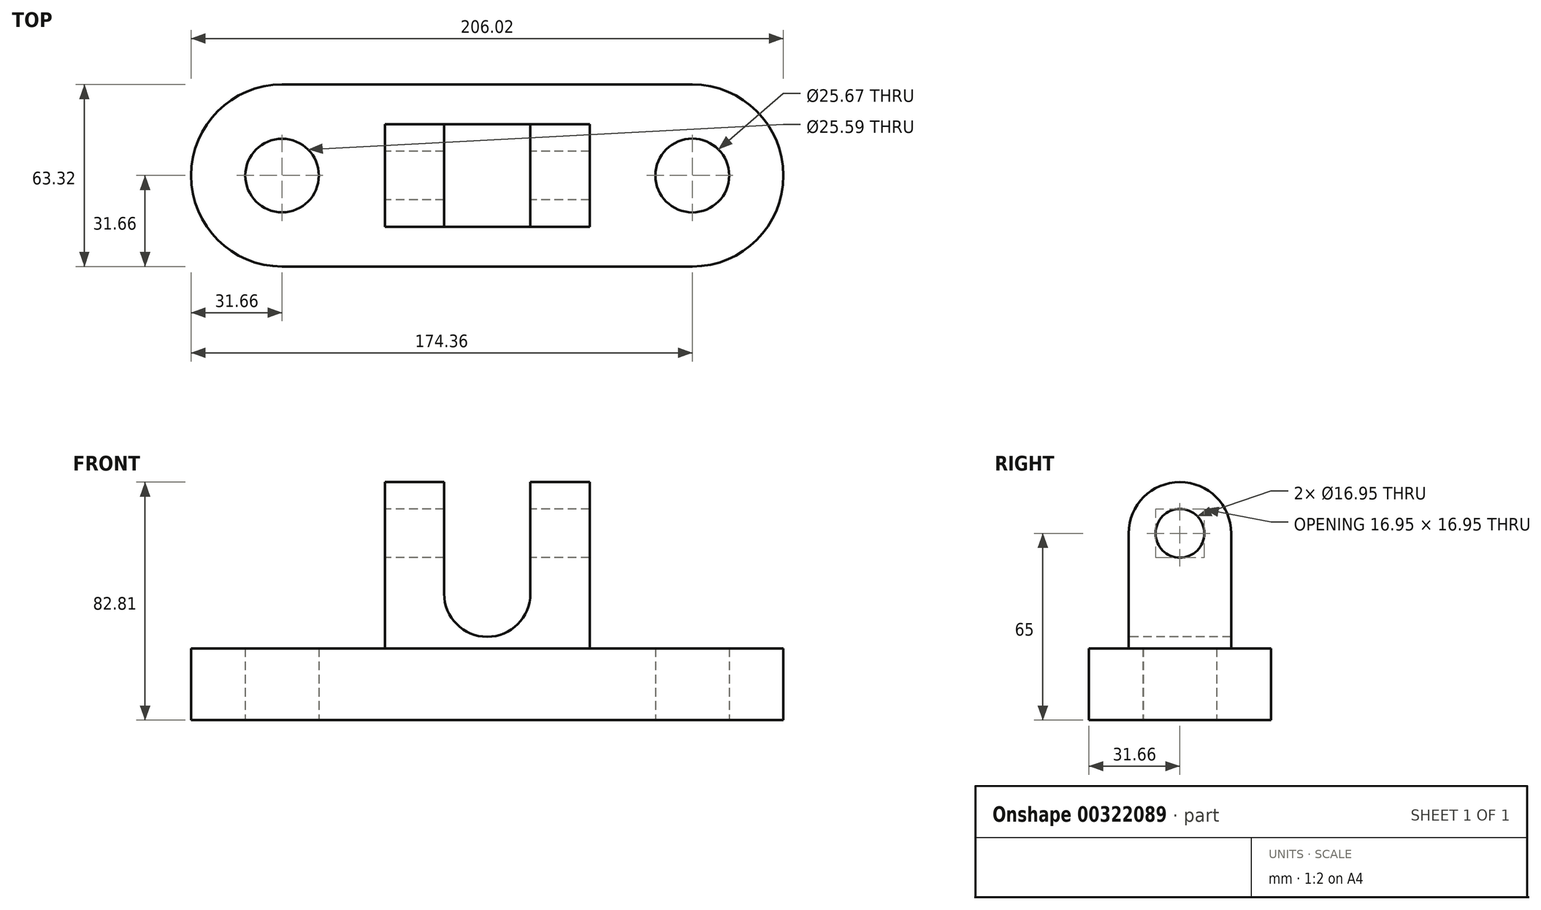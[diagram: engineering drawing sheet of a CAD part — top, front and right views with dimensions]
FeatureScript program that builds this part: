
annotation { "Feature Type Name" : "Feature", "Feature Type Description" : "" }
export const myFeature = defineFeature(function(context is Context, id is Id, definition is map)
    precondition{}
    {
        {
            var Q0;
            Q0=qCreatedBy(makeId("Top.planeOp"),FACE);
            var sketch = newSketch(context, id + "F0", { "sketchPlane" : qUnion([Q0])});
            skLineSegment(sketch, "E0.bottom", {"start": v(-71.35, 31.66) * mm, "end": v(71.35, 31.66) * mm});
            skLineSegment(sketch, "E0.top", {"start": v(-71.35, -31.66) * mm, "end": v(71.35, -31.66) * mm});
            skLineSegment(sketch, "E0.left", {"start": v(-71.35, 31.66) * mm, "end": v(-71.35, -31.66) * mm});
            skLineSegment(sketch, "E0.right", {"start": v(71.35, 31.66) * mm, "end": v(71.35, -31.66) * mm});
            skPoint(sketch, "E0.middle", {"position": v(0, 0) * mm});
            skCircle(sketch, "E1", {"center": v(71.35, 0) * mm, "radius": 31.66 * mm});
            skCircle(sketch, "E2", {"center": v(-71.35, 0) * mm, "radius": 31.66 * mm});
            skCircle(sketch, "E3", {"center": v(71.35, 0) * mm, "radius": 12.83 * mm});
            skCircle(sketch, "E4", {"center": v(-71.35, 0) * mm, "radius": 12.8 * mm});
            skSolve(sketch);
        }
        {
            var Q0;
            Q0 = qSketchRegion(id + "F0", true);
            extrude(context, id + "F1", {"entities" : qUnion([Q0]), "depth" : 25 * mm});
        }
        {
            var Q0;
            Q0=makeQuery(id+"F1.opExtrude","CAP_FACE",FACE,{"disambiguationData":[OSD([sQuery(id+"F0.wireOp",EDGE,"E0.bottom"),sQuery(id+"F0.wireOp",EDGE,"E0.top"),sQuery(id+"F0.wireOp",EDGE,"E1"),sQuery(id+"F0.wireOp",EDGE,"E2"),sQuery(id+"F0.wireOp",EDGE,"E3"),sQuery(id+"F0.wireOp",EDGE,"E4")])],"isStart":false});
            var sketch = newSketch(context, id + "F2", { "sketchPlane" : qUnion([Q0])});
            skLineSegment(sketch, "E5.bottom", {"start": v(35.62, -17.81) * mm, "end": v(-35.62, -17.81) * mm});
            skLineSegment(sketch, "E5.top", {"start": v(35.62, 17.81) * mm, "end": v(-35.62, 17.81) * mm});
            skLineSegment(sketch, "E5.left", {"start": v(35.62, -17.81) * mm, "end": v(35.62, 17.81) * mm});
            skLineSegment(sketch, "E5.right", {"start": v(-35.62, -17.81) * mm, "end": v(-35.62, 17.81) * mm});
            skPoint(sketch, "E5.middle", {"position": v(0, 0) * mm});
            skSolve(sketch);
        }
        {
            var Q0;
            Q0=makeQuery(id+"F2.imprint","IMPRINT",FACE,{"disambiguationData":[TD([[makeQuery(id+"F2.imprint","IMPRINT",EDGE,{"derivedFrom":sQuery(id+"F2.wireOp",EDGE,"E5.bottom")}),-1.0]])]});
            extrude(context, id + "F3", {"entities" : qUnion([Q0]), "operationType" : NewBodyOperationType.ADD, "depth" : 40 * mm});
        }
        {
            var Q0;
            Q0=makeQuery(id+"F3.opExtrude","SWEPT_FACE",FACE,{"disambiguationData":[OSD([sQuery(id+"F2.wireOp",EDGE,"E5.right")])]});
            var sketch = newSketch(context, id + "F4", { "sketchPlane" : qUnion([Q0])});
            skCircle(sketch, "E6", {"center": v(0, 65) * mm, "radius": 17.81 * mm});
            skCircle(sketch, "E7", {"center": v(0, 65) * mm, "radius": 8.48 * mm});
            skSolve(sketch);
        }
        {
            var Q0;
            {var subQ1=sQuery(id+"F2.wireOp",EDGE,"E5.right");var subQ2=makeQuery(id+"F3.opExtrude","CAP_EDGE",EDGE,{"disambiguationData":[OSD([subQ1])],"isStart":false});var subQ5=sQuery(id+"F4.wireOp",EDGE,"E7");var subQ6=makeQuery(id+"F4.imprint","INTERSECT",VERTEX,{"disambiguationData":[OD(0.0)],"derivedFrom":[subQ2,subQ5]});Q0=makeQuery(id+"F4.imprint","IMPRINT",FACE,{"disambiguationData":[TD([[makeQuery(id+"F4.imprint","IMPRINT",EDGE,{"disambiguationData":[TD([[subQ6,-1.0]])],"derivedFrom":subQ5}),-1.0]])]});}
            var Q1;
            Q1=makeQuery(id+"F3.opExtrude","SWEPT_FACE",FACE,{"disambiguationData":[OSD([sQuery(id+"F2.wireOp",EDGE,"E5.left")])]});
            extrude(context, id + "F5", {"entities" : qUnion([Q0]), "operationType" : NewBodyOperationType.ADD, "endBound" : BoundingType.UP_TO_SURFACE, "oppositeDirection" : true, "endBoundEntityFace" : qUnion([Q1]), "depth" : 25 * mm});
        }
        {
            var Q0;
            {var subQ0=sQuery(id+"F4.wireOp",EDGE,"E7");var subQ1=makeQuery(id+"F3.opExtrude","CAP_EDGE",EDGE,{"disambiguationData":[OSD([sQuery(id+"F2.wireOp",EDGE,"E5.right")])],"isStart":false});var subQ2=makeQuery(id+"F4.imprint","INTERSECT",VERTEX,{"disambiguationData":[OD(0.0)],"derivedFrom":[subQ1,subQ0]});Q0=makeQuery(id+"F4.imprint","IMPRINT",FACE,{"disambiguationData":[TD([[makeQuery(id+"F4.imprint","IMPRINT",EDGE,{"disambiguationData":[TD([[subQ2,1.0]])],"derivedFrom":subQ0}),1.0]])]});}
            extrude(context, id + "F6", {"entities" : qUnion([Q0]), "operationType" : NewBodyOperationType.REMOVE, "endBound" : BoundingType.UP_TO_NEXT, "oppositeDirection" : true, "depth" : 25 * mm});
        }
        {
            var Q0;
            Q0=makeQuery(id+"F3.opExtrude","SWEPT_FACE",FACE,{"disambiguationData":[OSD([sQuery(id+"F2.wireOp",EDGE,"E5.bottom")])]});
            var sketch = newSketch(context, id + "F7", { "sketchPlane" : qUnion([Q0])});
            skCircle(sketch, "E8", {"center": v(0, 44) * mm, "radius": 15 * mm});
            skLineSegment(sketch, "E9.bottom", {"start": v(15, 44) * mm, "end": v(-15, 44) * mm});
            skLineSegment(sketch, "E9.top", {"start": v(15, 84) * mm, "end": v(-15, 84) * mm});
            skLineSegment(sketch, "E9.left", {"start": v(15, 44) * mm, "end": v(15, 84) * mm});
            skLineSegment(sketch, "E9.right", {"start": v(-15, 44) * mm, "end": v(-15, 84) * mm});
            skPoint(sketch, "E9.middle", {"position": v(0, 64) * mm});
            skPoint(sketch, "E9.middle.positionSnap0", {"position": v(0, 65) * mm});
            skPoint(sketch, "E9.centerSnap0", {"position": v(0, 65) * mm});
            skSolve(sketch);
        }
        {
            var Q0;
            {var subQ0=sQuery(id+"F7.wireOp",EDGE,"E9.top");Q0=makeQuery(id+"F7.imprint","IMPRINT",FACE,{"disambiguationData":[TD([[makeQuery(id+"F7.imprint","IMPRINT",EDGE,{"derivedFrom":subQ0}),1.0]])]});}
            var Q1;
            {var subQ0=sQuery(id+"F7.wireOp",EDGE,"E9.left");var subQ1=sQuery(id+"F7.wireOp",EDGE,"E9.bottom");var subQ2=sQuery(id+"F7.wireOp",EDGE,"E8");var subQ3=makeQuery(id+"F7.imprint","INTERSECT",VERTEX,{"derivedFrom":[subQ2,subQ1,subQ0]});Q1=makeQuery(id+"F7.imprint","IMPRINT",FACE,{"disambiguationData":[TD([[makeQuery(id+"F7.imprint","IMPRINT",EDGE,{"disambiguationData":[TD([[subQ3,-1.0]])],"derivedFrom":subQ2}),-1.0]])]});}
            var Q2;
            {var subQ0=sQuery(id+"F7.wireOp",EDGE,"E9.bottom");Q2=makeQuery(id+"F7.imprint","IMPRINT",FACE,{"disambiguationData":[TD([[makeQuery(id+"F7.imprint","IMPRINT",EDGE,{"derivedFrom":subQ0}),-1.0]])]});}
            var Q3;
            {var subQ0=sQuery(id+"F7.wireOp",EDGE,"E9.bottom");Q3=makeQuery(id+"F7.imprint","IMPRINT",FACE,{"disambiguationData":[TD([[makeQuery(id+"F7.imprint","IMPRINT",EDGE,{"derivedFrom":subQ0}),1.0]])]});}
            extrude(context, id + "F8", {"entities" : qUnion([Q0, Q1, Q2, Q3]), "operationType" : NewBodyOperationType.REMOVE, "endBound" : BoundingType.THROUGH_ALL, "oppositeDirection" : true, "depth" : 25 * mm});
        }
    });
